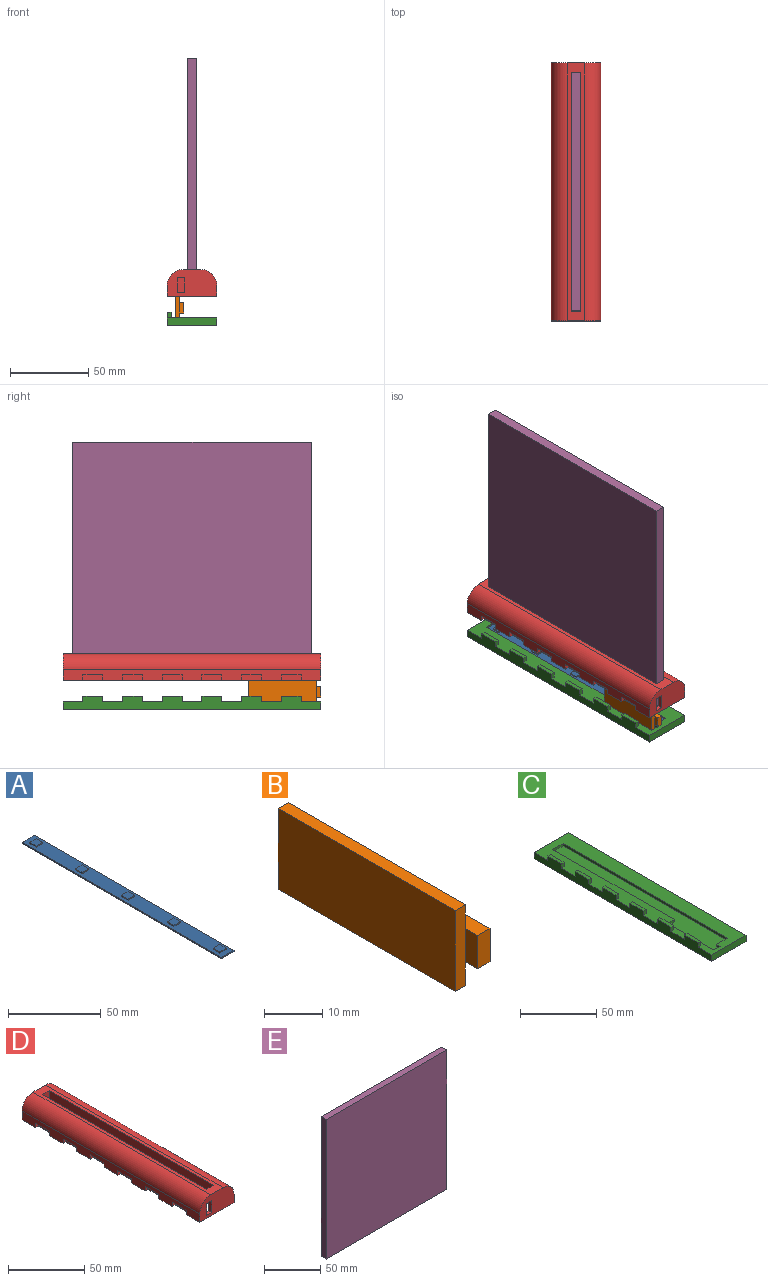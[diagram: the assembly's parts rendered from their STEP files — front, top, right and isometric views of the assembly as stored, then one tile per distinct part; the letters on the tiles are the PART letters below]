
ASSEMBLY  parts=5 mates=11
PART A: 31 faces, bbox 9.5x152.4x1.6 mm
  f0: plane 152.4x9.53mm, normal (0,0,1), area 1326.6mm2, adj f1,f2,f3,f4,f6,f7,f8,f9
  f1: plane 9.53x0.79mm, normal (0,1,0), area 7.6mm2, adj f0,f2,f4,f5
  f2: plane 152.4x0.79mm, normal (-1,0,0), area 121mm2, adj f0,f1,f3,f5
  f3: plane 9.53x0.79mm, normal (0,-1,0), area 7.6mm2, adj f0,f2,f4,f5
  f4: plane 152.4x0.79mm, normal (1,0,0), area 121mm2, adj f0,f1,f3,f5
  f5: plane 152.4x9.53mm, normal (0,0,-1), area 1451.6mm2, adj f1,f2,f3,f4
  f6: plane 5x0.79mm, normal (-1,0,0), area 4mm2, adj f0,f7,f9,f10
  f7: plane 5x0.79mm, normal (0,-1,0), area 4mm2, adj f0,f6,f8,f10
  f8: plane 5x0.79mm, normal (1,0,0), area 4mm2, adj f0,f7,f9,f10
  f9: plane 5x0.79mm, normal (0,1,0), area 4mm2, adj f0,f6,f8,f10
  f10: plane 5x5mm, normal (0,0,1), area 25mm2, adj f6,f7,f8,f9
  f11: plane 5x0.79mm, normal (-1,0,0), area 4mm2, adj f0,f12,f14,f15
  f12: plane 5x0.79mm, normal (0,-1,0), area 4mm2, adj f0,f11,f13,f15
  f13: plane 5x0.79mm, normal (1,0,0), area 4mm2, adj f0,f12,f14,f15
  f14: plane 5x0.79mm, normal (0,1,0), area 4mm2, adj f0,f11,f13,f15
  f15: plane 5x5mm, normal (0,0,1), area 25mm2, adj f11,f12,f13,f14
  f16: plane 5x0.79mm, normal (-1,0,0), area 4mm2, adj f0,f17,f19,f20
  f17: plane 5x0.79mm, normal (0,-1,0), area 4mm2, adj f0,f16,f18,f20
  f18: plane 5x0.79mm, normal (1,0,0), area 4mm2, adj f0,f17,f19,f20
  f19: plane 5x0.79mm, normal (0,1,0), area 4mm2, adj f0,f16,f18,f20
  f20: plane 5x5mm, normal (0,0,1), area 25mm2, adj f16,f17,f18,f19
  f21: plane 5x0.79mm, normal (0,1,0), area 4mm2, adj f0,f22,f24,f25
  f22: plane 5x0.79mm, normal (-1,0,0), area 4mm2, adj f0,f21,f23,f25
  f23: plane 5x0.79mm, normal (0,-1,0), area 4mm2, adj f0,f22,f24,f25
  f24: plane 5x0.79mm, normal (1,0,0), area 4mm2, adj f0,f21,f23,f25
  f25: plane 5x5mm, normal (0,0,1), area 25mm2, adj f21,f22,f23,f24
  f26: plane 5x0.79mm, normal (0,1,0), area 4mm2, adj f0,f27,f29,f30
  f27: plane 5x0.79mm, normal (-1,0,0), area 4mm2, adj f0,f26,f28,f30
  f28: plane 5x0.79mm, normal (0,-1,0), area 4mm2, adj f0,f27,f29,f30
  f29: plane 5x0.79mm, normal (1,0,0), area 4mm2, adj f0,f26,f28,f30
  f30: plane 5x5mm, normal (0,0,1), area 25mm2, adj f26,f27,f28,f29
PART B: 12 faces, bbox 5.5x46x17 mm
  f0: plane 43x17mm, normal (1,0,0), area 689mm2, adj f1,f2,f3,f4,f6,f8,f9
  f1: plane 17x2.5mm, normal (0,-1,0), area 42.5mm2, adj f0,f2,f4,f5,f11
  f2: plane 43x2.5mm, normal (0,0,-1), area 107.5mm2, adj f0,f1,f3,f5
  f3: plane 17x2.5mm, normal (0,1,0), area 42.5mm2, adj f0,f2,f4,f5
  f4: plane 43x2.5mm, normal (0,0,1), area 107.5mm2, adj f0,f1,f3,f5
  f5: plane 43x17mm, normal (-1,0,0), area 731mm2, adj f1,f2,f3,f4
  f6: plane 9x3mm, normal (0,0,1), area 27mm2, adj f0,f7,f9,f10,f11
  f7: plane 7x3mm, normal (0,-1,0), area 21mm2, adj f6,f8,f10,f11
  f8: plane 9x3mm, normal (0,0,-1), area 27mm2, adj f0,f7,f9,f10,f11
  f9: plane 7x3mm, normal (0,1,0), area 21mm2, adj f0,f6,f8,f10
  f10: plane 9x7mm, normal (1,0,0), area 63mm2, adj f6,f7,f8,f9
  f11: plane 7x3mm, normal (-1,0,0), area 21mm2, adj f1,f6,f7,f8
PART C: 39 faces, bbox 31.8x165.1x8.6 mm
  f0: plane 165.1x31.75mm, normal (0,0,1), area 3339mm2, adj f1,f2,f4,f5,f6,f7,f8,f9
  f1: plane 112.71x1.91mm, normal (1,0,0), area 214.7mm2, adj f0,f7,f10,f11
  f2: plane 165.1x8.57mm, normal (-1,0,0), area 1104.8mm2, adj f0,f3,f5,f6,f15,f16,f17,f19
  f3: plane 165.1x31.75mm, normal (0,0,-1), area 5241.9mm2, adj f2,f4,f5,f6
  f4: plane 165.1x5.08mm, normal (1,0,0), area 838.7mm2, adj f0,f3,f5,f6
  f5: plane 31.75x5.08mm, normal (0,-1,0), area 161.3mm2, adj f0,f2,f3,f4
  f6: plane 31.75x5.08mm, normal (0,1,0), area 161.3mm2, adj f0,f2,f3,f4
  f7: plane 9.53x1.91mm, normal (0,-1,0), area 18.1mm2, adj f0,f1,f9,f10
  f8: plane 9.79x1.91mm, normal (0,1,0), area 18.6mm2, adj f0,f9,f10,f14
  f9: plane 152.4x1.91mm, normal (-1,0,0), area 290.3mm2, adj f0,f7,f8,f10
  f10: plane 155.58x15.56mm, normal (0,0,1), area 1709.3mm2, adj f1,f7,f8,f9,f11,f12,f13,f14
  f11: plane 6.03x1.91mm, normal (0,-1,0), area 11.5mm2, adj f0,f1,f10,f12
  f12: plane 42.86x1.91mm, normal (1,0,0), area 81.7mm2, adj f0,f10,f11,f13
  f13: plane 5.77x1.91mm, normal (0,1,0), area 11mm2, adj f0,f10,f12,f14
  f14: plane 3.18x1.91mm, normal (-1,0,0), area 6mm2, adj f0,f8,f10,f13
  f15: plane 12.7x2.54mm, normal (0,0,1), area 32.3mm2, adj f2,f16,f17,f18
  f16: plane 3.49x2.54mm, normal (0,1,0), area 8.9mm2, adj f0,f2,f15,f18
  f17: plane 3.49x2.54mm, normal (0,-1,0), area 8.9mm2, adj f0,f2,f15,f18
  f18: plane 12.7x3.49mm, normal (1,0,0), area 44.4mm2, adj f0,f15,f16,f17
  f19: plane 12.7x2.54mm, normal (0,0,1), area 32.3mm2, adj f2,f20,f21,f22
  f20: plane 3.49x2.54mm, normal (0,1,0), area 8.9mm2, adj f0,f2,f19,f22
  f21: plane 3.49x2.54mm, normal (0,-1,0), area 8.9mm2, adj f0,f2,f19,f22
  f22: plane 12.7x3.49mm, normal (1,0,0), area 44.4mm2, adj f0,f19,f20,f21
  f23: plane 12.7x2.54mm, normal (0,0,1), area 32.3mm2, adj f2,f24,f25,f26
  f24: plane 3.49x2.54mm, normal (0,1,0), area 8.9mm2, adj f0,f2,f23,f26
  f25: plane 3.49x2.54mm, normal (0,-1,0), area 8.9mm2, adj f0,f2,f23,f26
  f26: plane 12.7x3.49mm, normal (1,0,0), area 44.4mm2, adj f0,f23,f24,f25
  f27: plane 12.7x2.54mm, normal (0,0,1), area 32.3mm2, adj f2,f28,f29,f30
  f28: plane 3.49x2.54mm, normal (0,1,0), area 8.9mm2, adj f0,f2,f27,f30
  f29: plane 3.49x2.54mm, normal (0,-1,0), area 8.9mm2, adj f0,f2,f27,f30
  f30: plane 12.7x3.49mm, normal (1,0,0), area 44.4mm2, adj f0,f27,f28,f29
  f31: plane 12.7x2.54mm, normal (0,0,1), area 32.3mm2, adj f2,f32,f33,f34
  f32: plane 3.49x2.54mm, normal (0,1,0), area 8.9mm2, adj f0,f2,f31,f34
  f33: plane 3.49x2.54mm, normal (0,-1,0), area 8.9mm2, adj f0,f2,f31,f34
  f34: plane 12.7x3.49mm, normal (1,0,0), area 44.4mm2, adj f0,f31,f32,f33
  f35: plane 12.7x2.54mm, normal (0,0,1), area 32.3mm2, adj f2,f36,f37,f38
  f36: plane 3.49x2.54mm, normal (0,1,0), area 8.9mm2, adj f0,f2,f35,f38
  f37: plane 3.49x2.54mm, normal (0,-1,0), area 8.9mm2, adj f0,f2,f35,f38
  f38: plane 12.7x3.49mm, normal (1,0,0), area 44.4mm2, adj f0,f35,f36,f37
PART D: 47 faces, bbox 31.8x165.1x17.1 mm
  f0: plane 165.1x6.99mm, normal (-1,0,0), area 887.1mm2, adj f2,f6,f7,f8,f23,f24,f25,f27
  f1: plane 152.4x17.15mm, normal (1,0,0), area 1806.4mm2, adj f2,f3,f9,f10,f13,f16
  f2: plane 165.1x31.75mm, normal (0,0,-1), area 3668mm2, adj f0,f1,f4,f7,f8,f9,f10,f11
  f3: plane 165.1x11.43mm, normal (0,0,1), area 919.4mm2, adj f1,f5,f6,f7,f8,f9,f10,f11
  f4: plane 165.1x6.99mm, normal (1,0,0), area 1153.2mm2, adj f2,f5,f7,f8
  f5: cylinder r=10.16mm len=165.1mm, axis (0,1,0), area 2634.9mm2, adj f3,f4,f7,f8
  f6: cylinder r=10.16mm len=165.1mm, axis (0,1,0), area 2634.9mm2, adj f0,f3,f7,f8
  f7: plane 31.75x17.15mm, normal (0,-1,0), area 454.7mm2, adj f0,f2,f3,f4,f5,f6,f17,f18
  f8: plane 31.75x17.15mm, normal (0,1,0), area 500mm2, adj f0,f2,f3,f4,f5,f6
  f9: plane 17.15x6.35mm, normal (0,-1,0), area 108.9mm2, adj f1,f2,f3,f11
  f10: plane 17.15x6.35mm, normal (0,1,0), area 68.5mm2, adj f1,f2,f3,f11,f13,f22
  f11: plane 152.4x17.15mm, normal (-1,0,0), area 2612.9mm2, adj f2,f3,f9,f10
  f12: plane 15.88x0.64mm, normal (-1,0,0), area 10.1mm2, adj f2,f13,f21,f22
  f13: plane 53.98x7.62mm, normal (0,0,-1), area 275.6mm2, adj f1,f10,f12,f14,f16,f21,f22
  f14: cylinder r=2.54mm len=53.98mm, axis (0,-1,0), area 215.4mm2, adj f13,f15,f16,f21
  f15: plane 53.98x13.34mm, normal (1,0,0), area 719.8mm2, adj f2,f14,f16,f21
  f16: plane 15.88x7.62mm, normal (0,-1,0), area 119.6mm2, adj f1,f2,f13,f14,f15
  f17: plane 9.53x3.18mm, normal (-1,0,0), area 30.2mm2, adj f7,f18,f20,f21
  f18: plane 4.76x3.18mm, normal (0,0,1), area 15.1mm2, adj f7,f17,f19,f21
  f19: plane 9.53x3.18mm, normal (1,0,0), area 30.2mm2, adj f7,f18,f20,f21
  f20: plane 4.76x3.18mm, normal (0,0,-1), area 15.1mm2, adj f7,f17,f19,f21
  f21: plane 15.88x7.62mm, normal (0,1,0), area 74.2mm2, adj f2,f12,f13,f14,f15,f17,f18,f19
  f22: cylinder r=2.54mm len=15.88mm, axis (0,0,1), area 63.3mm2, adj f2,f10,f12,f13
  f23: plane 12.7x2.54mm, normal (0,0,-1), area 32.3mm2, adj f0,f24,f25,f26
  f24: plane 3.49x2.54mm, normal (0,-1,0), area 8.9mm2, adj f0,f2,f23,f26
  f25: plane 3.49x2.54mm, normal (0,1,0), area 8.9mm2, adj f0,f2,f23,f26
  f26: plane 12.7x3.49mm, normal (-1,0,0), area 44.4mm2, adj f2,f23,f24,f25
  f27: plane 12.7x2.54mm, normal (0,0,-1), area 32.3mm2, adj f0,f28,f29,f30
  f28: plane 3.49x2.54mm, normal (0,-1,0), area 8.9mm2, adj f0,f2,f27,f30
  f29: plane 3.49x2.54mm, normal (0,1,0), area 8.9mm2, adj f0,f2,f27,f30
  f30: plane 12.7x3.49mm, normal (-1,0,0), area 44.4mm2, adj f2,f27,f28,f29
  f31: plane 12.7x2.54mm, normal (0,0,-1), area 32.3mm2, adj f0,f32,f33,f34
  f32: plane 3.49x2.54mm, normal (0,-1,0), area 8.9mm2, adj f0,f2,f31,f34
  f33: plane 3.49x2.54mm, normal (0,1,0), area 8.9mm2, adj f0,f2,f31,f34
  f34: plane 12.7x3.49mm, normal (-1,0,0), area 44.4mm2, adj f2,f31,f32,f33
  f35: plane 12.7x2.54mm, normal (0,0,-1), area 32.3mm2, adj f0,f36,f37,f38
  f36: plane 3.49x2.54mm, normal (0,-1,0), area 8.9mm2, adj f0,f2,f35,f38
  f37: plane 3.49x2.54mm, normal (0,1,0), area 8.9mm2, adj f0,f2,f35,f38
  f38: plane 12.7x3.49mm, normal (-1,0,0), area 44.4mm2, adj f2,f35,f36,f37
  f39: plane 12.7x2.54mm, normal (0,0,-1), area 32.3mm2, adj f0,f40,f41,f42
  f40: plane 3.49x2.54mm, normal (0,-1,0), area 8.9mm2, adj f0,f2,f39,f42
  f41: plane 3.49x2.54mm, normal (0,1,0), area 8.9mm2, adj f0,f2,f39,f42
  f42: plane 12.7x3.49mm, normal (-1,0,0), area 44.4mm2, adj f2,f39,f40,f41
  f43: plane 12.7x2.54mm, normal (0,0,-1), area 32.3mm2, adj f0,f44,f45,f46
  f44: plane 3.49x2.54mm, normal (0,-1,0), area 8.9mm2, adj f0,f2,f43,f46
  f45: plane 3.49x2.54mm, normal (0,1,0), area 8.9mm2, adj f0,f2,f43,f46
  f46: plane 12.7x3.49mm, normal (-1,0,0), area 44.4mm2, adj f2,f43,f44,f45
PART E: 6 faces, bbox 152.4x6.4x152.4 mm
  f0: plane 152.4x6.35mm, normal (-1,0,0), area 967.7mm2, adj f1,f3,f4,f5
  f1: plane 152.4x6.35mm, normal (0,0,-1), area 967.7mm2, adj f0,f2,f4,f5
  f2: plane 152.4x6.35mm, normal (1,0,0), area 967.7mm2, adj f1,f3,f4,f5
  f3: plane 152.4x6.35mm, normal (0,0,1), area 967.7mm2, adj f0,f2,f4,f5
  f4: plane 152.4x152.4mm, normal (0,-1,0), area 23225.8mm2, adj f0,f1,f2,f3
  f5: plane 152.4x152.4mm, normal (0,1,0), area 23225.8mm2, adj f0,f1,f2,f3
PLACE A t=(-50.63,11.8,-9.55)mm
PLACE B t=(-60.18,-45.77,-17.8)mm
PLACE C t=(-50.63,11.8,-12.72)mm fixed
PLACE D t=(-50.63,11.8,6.18)mm
PLACE E rot(axis=(0,0,-1),90deg) t=(-50.63,11.8,6.18)mm
MATE planar D.f7 <-> C.f5  axis (0,-1,0) through (-49.92,-70.75,14.28)mm
MATE planar B.f2 <-> C.f10  axis (0,0,-1) through (-60.18,-46.07,-9.55)mm
MATE planar A.f5 <-> C.f10  axis (0,0,-1) through (-50.63,11.8,-9.55)mm
MATE planar D.f0 <-> C.f2  axis (-1,0,0) through (-66.51,-58.05,9.68)mm
MATE planar D.f9 <-> E.f0  axis (0,-1,0) through (-50.63,88,14.76)mm
MATE planar D.f2 <-> E.f1  axis (0,0,-1) through (-47.46,11.8,6.18)mm
MATE planar B.f1 <-> C.f13  axis (0,-1,0) through (-60.18,-67.57,-1.05)mm
MATE planar B.f5 <-> C.f12  axis (-1,0,0) through (-61.43,-46.07,-1.05)mm
MATE planar C.f7 <-> A.f1  axis (0,-1,0) through (-50.63,88,-8.6)mm
MATE planar E.f4 <-> D.f1  axis (-1,0,0) through (-53.81,11.8,82.38)mm
MATE planar C.f9 <-> A.f4  axis (-1,0,0) through (-45.87,11.8,-8.6)mm
